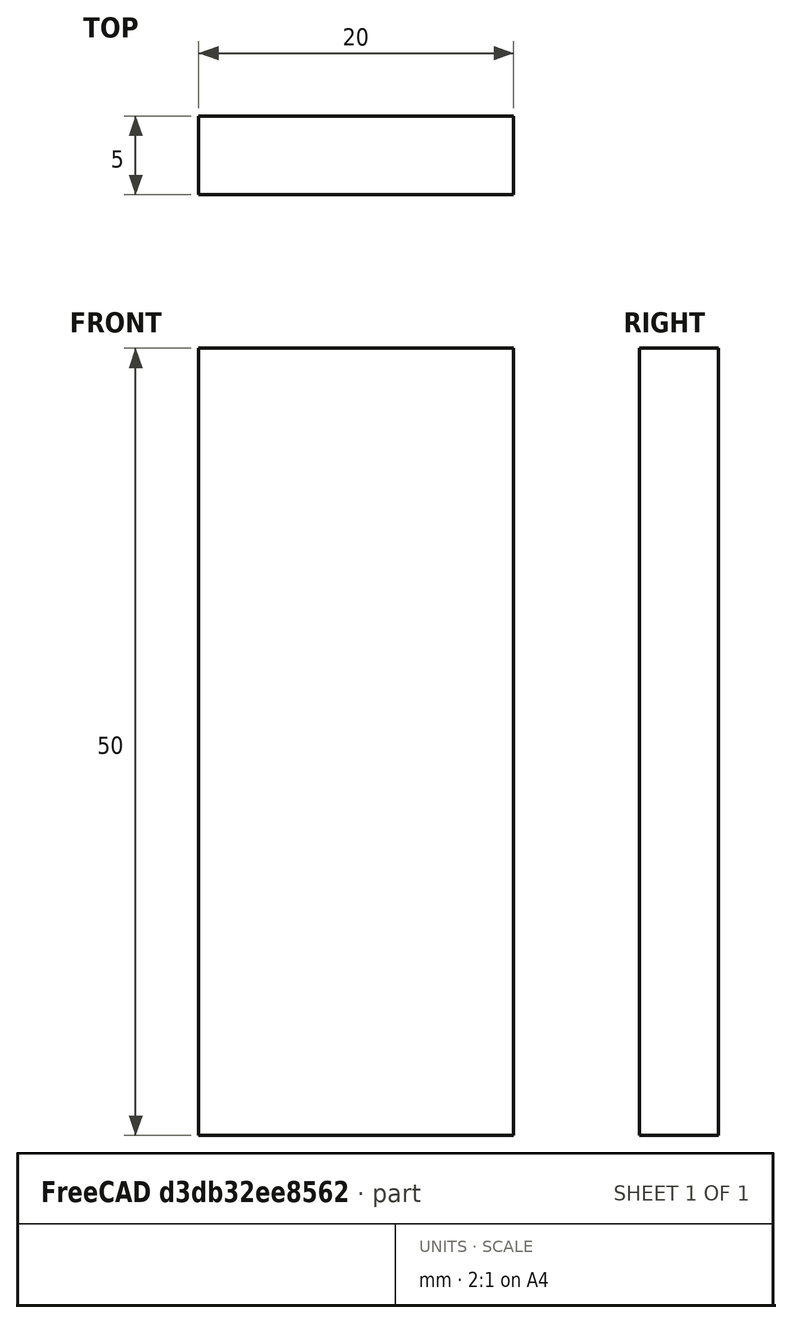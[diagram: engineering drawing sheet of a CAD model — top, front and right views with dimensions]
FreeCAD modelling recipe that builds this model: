
FCSTD DOCUMENT  (FreeCAD 0.15R4671 (Git))
Label: Flat Bar 20x5 EN10058 S235JR
License: All rights reserved
LicenseURL: http://en.wikipedia.org/wiki/All_rights_reserved
objects: Sketcher::SketchObject×1, Part::Extrusion×1
note: 2 computed .brp shape members not serialized (recipe doc carries the construction recipe); baked Part::Feature solids carry a one-line shape summary decoded from their .brp

FEATURE [Sketcher::SketchObject] Sketch
  sketch-geometry (4):
    g0: LineSegment StartX=-10 StartY=-2.5 StartZ=0 EndX=10 EndY=-2.5 EndZ=0
    g1: LineSegment StartX=10 StartY=-2.5 StartZ=0 EndX=10 EndY=2.5 EndZ=0
    g2: LineSegment StartX=10 StartY=2.5 StartZ=0 EndX=-10 EndY=2.5 EndZ=0
    g3: LineSegment StartX=-10 StartY=2.5 StartZ=0 EndX=-10 EndY=-2.5 EndZ=0
  constraints (12):
    c: Coincident(g0,g1)
    c: Coincident(g1,g2)
    c: Coincident(g2,g3)
    c: Coincident(g3,g0)
    c: Horizontal(g0)
    c: Horizontal(g2)
    c: Vertical(g1)
    c: Vertical(g3)
    c: Symmetric(g1,g2,g-2)
    c: Symmetric(g0,g1,g-1)
    c: DistanceY(g1) = 5
    c: DistanceX(g0) = 20
FEATURE [Part::Extrusion] Extrude  label="Flat Bar 20x5 EN10058 S235JR"
  Base = -> Sketch
  Dir = (0,0,50)
  Solid = true
